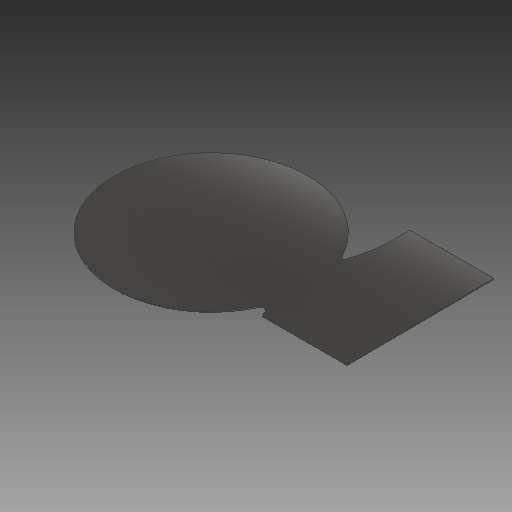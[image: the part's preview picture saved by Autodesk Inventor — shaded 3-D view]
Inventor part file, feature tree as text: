
AUTODESK INVENTOR PART (.ipt)
format: ipt  version: 2018 (Build 220112000, 112)  size: 121,344 bytes
history: native  units: mm
features: plane x1, extrude x1, sketch x1
ambient origin geometry x8: Origin, YZ Plane, XZ Plane, XY Plane, X Axis, Y Axis, Z Axis, Center Point
bodies: Volumenkörper1 (feature_tree)
feature tree (3):
  plane  "Arbeitsebene7"
  extrude  "Extrusion6"  Depth=1.0mm
  sketch  "Skizze6"  dims[d3=4.5mm d5=8.0mm d22=165.0mm d24=2.0mm d25=2.0mm d26=1.0mm d27=0.0mm]
